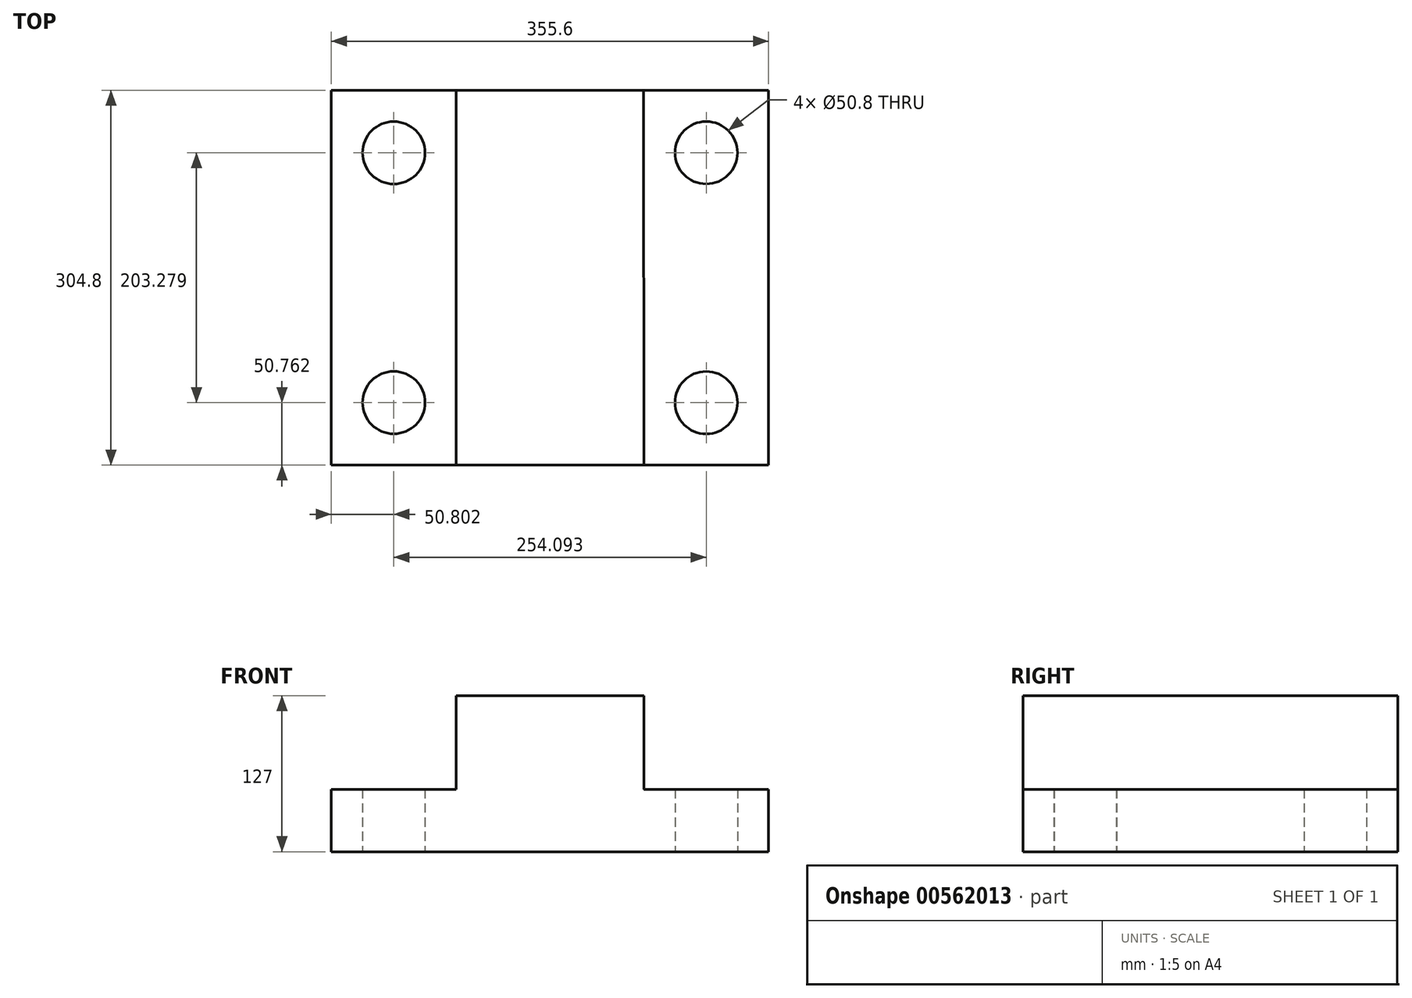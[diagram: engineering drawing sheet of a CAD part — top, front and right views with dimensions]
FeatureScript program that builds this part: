
annotation { "Feature Type Name" : "Feature", "Feature Type Description" : "" }
export const myFeature = defineFeature(function(context is Context, id is Id, definition is map)
    precondition{}
    {
        {
            var Q0;
            Q0=qCreatedBy(makeId("Top.planeOp"),FACE);
            var sketch = newSketch(context, id + "F0", { "sketchPlane" : qUnion([Q0])});
            skLineSegment(sketch, "E0.bottom", {"start": v(54.28, 208.5) * mm, "end": v(409.88, 208.5) * mm});
            skLineSegment(sketch, "E0.top", {"start": v(54.28, -96.3) * mm, "end": v(409.88, -96.3) * mm});
            skLineSegment(sketch, "E0.left", {"start": v(54.28, 208.5) * mm, "end": v(54.28, -96.3) * mm});
            skLineSegment(sketch, "E0.right", {"start": v(409.88, 208.5) * mm, "end": v(409.88, -96.3) * mm});
            skLineSegment(sketch, "E1", {"start": v(155.88, -96.3) * mm, "end": v(155.88, 208.5) * mm});
            skLineSegment(sketch, "E2", {"start": v(308.34, 208.5) * mm, "end": v(308.5, -96.3) * mm});
            skCircle(sketch, "E3", {"center": v(105.08, 157.71) * mm, "radius": 25.4 * mm});
            skCircle(sketch, "E4", {"center": v(105.08, -45.5) * mm, "radius": 25.4 * mm});
            skCircle(sketch, "E5", {"center": v(359.18, -45.54) * mm, "radius": 25.4 * mm});
            skCircle(sketch, "E6", {"center": v(359.17, 157.74) * mm, "radius": 25.4 * mm});
            skSolve(sketch);
        }
        {
            var Q0;
            {var subQ0=sQuery(id+"F0.wireOp",EDGE,"E1");Q0=makeQuery(id+"F0.imprint","IMPRINT",FACE,{"disambiguationData":[TD([[makeQuery(id+"F0.imprint","IMPRINT",EDGE,{"derivedFrom":subQ0}),-1.0]])]});}
            extrude(context, id + "F1", {"entities" : qUnion([Q0]), "depth" : 127 * mm, "offsetDistance" : 25.4 * mm});
        }
        {
            var Q0;
            Q0 = qSketchRegion(id + "F0", true);
            extrude(context, id + "F2", {"entities" : qUnion([Q0]), "operationType" : NewBodyOperationType.ADD, "depth" : 50.8 * mm, "offsetDistance" : 25.4 * mm});
        }
    });
